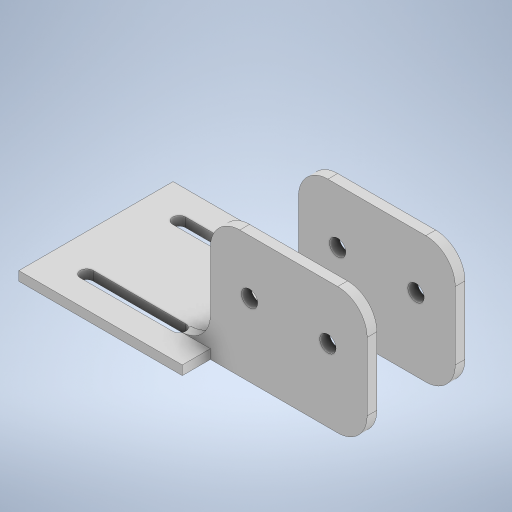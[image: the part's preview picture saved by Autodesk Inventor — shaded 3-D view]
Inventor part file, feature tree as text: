
AUTODESK INVENTOR PART (.ipt)
format: ipt  version: 2024 (Build 280153000, 153)  size: 513,024 bytes
history: native  units: in
note: dims shown in document units (in); Inventor stores cm internally (conversion verified against a paired STEP export)
features: sketch x24, extrude x23, projected_geometry x6, fillet x3
ambient origin geometry x8: Origin, YZ Plane, XZ Plane, XY Plane, X Axis, Y Axis, Z Axis, Center Point
bodies: Solid1 (feature_tree)
feature tree (56):
  extrude  "Extrusion1"  Depth=1.9685in
  extrude  "Extrusion2"  Depth=0.1181in
  extrude  "Extrusion3"  Depth=0.4331in
  extrude  "Extrusion4"  Depth=1.1811in
  extrude  "Extrusion5"  Depth=0.165in
  extrude  "Extrusion6"  Depth=0.165in
  extrude  "Extrusion7"  Depth=0.3935in
  extrude  "Extrusion8"  Depth=0.4921in TaperAngle=0.0deg
  extrude  "Extrusion9"  Depth=0.125in
  extrude  "Extrusion10"  Depth=1.0in
  extrude  "Extrusion11"  Depth=1.667in TaperAngle=0.0deg
  extrude  "Extrusion12"  Depth=1.2705in TaperAngle=0.0deg
  extrude  "Extrusion13"  Depth=0.125in
  extrude  "Extrusion14"  Depth=1.0in
  extrude  "Extrusion15"  Depth=2.9375in TaperAngle=0.0deg
  extrude  "Extrusion16"  Depth=2.0625in TaperAngle=0.0deg
  extrude  "Extrusion17"  Depth=1.0in
  fillet  "Fillet1"  Radius=1.0in
  sketch  "Sketch18"  dims[d48=0.207in d49=0.207in]
  extrude  "Extrusion18"  Depth=0.207in
  sketch  "Sketch20"  dims[d54=1.0in d55=0.4845in]
  extrude  "Extrusion19"  Depth=0.425in TaperAngle=0.0deg
  extrude  "Extrusion20"  Depth=1.0in
  extrude  "Extrusion21"  Depth=0.125in
  fillet  "Fillet2"  Radius=0.125in
  sketch  "Sketch23"  dims[d63=0.375in d64=0.5in d65=1.0in]
  extrude  "Extrusion22"  Depth=1.5in TaperAngle=0.0deg
  extrude  "Extrusion23"  Depth=1.0in
  fillet  "Fillet3"  Radius=1.0in
  sketch  "Sketch1"  dims[d0=2.0866in d1=1.9685in]
  sketch  "Sketch2"  dims[d2=0.1181in d3=0.0in d4=0.1181in]
  sketch  "Sketch3"  dims[d5=2.0079in d6=0.0in d7=0.4331in]
  sketch  "Sketch4"  dims[d8=0.1654in d9=1.1811in]
  sketch  "Sketch5"  dims[d10=0.165in d11=0.433in]
  sketch  "Sketch6"  dims[d12=0.165in d13=0.165in]
  sketch  "Sketch7"  dims[d14=1.1811in d15=0.3935in]
  projected_geometry  "Projected Loop1"
  sketch  "Sketch8"  dims[d16=0.3939in d17=0.4921in d18=0.0in]
  sketch  "Sketch9"  dims[d19=0.875in d20=0.0in d21=0.125in]
  sketch  "Sketch10"  dims[d22=0.125in d23=1.0in]
  sketch  "Sketch11"  dims[d24=0.36in d25=1.667in d26=0.0in]
  projected_geometry  "Projected Loop2"
  projected_geometry  "Projected Loop3"
  sketch  "Sketch12"  dims[d27=0.667in d28=1.2705in d29=0.0in]
  sketch  "Sketch13"  dims[d30=0.125in d31=0.0in d32=0.125in]
  sketch  "Sketch14"  dims[d33=1.0in d34=0.0in d35=0.34in]
  sketch  "Sketch15"  dims[d36=0.4375in d37=0.0in d38=2.9375in d39=0.0in]
  projected_geometry  "Projected Loop4"
  sketch  "Sketch16"  dims[d40=3.3125in d41=0.0in d42=2.0625in d43=0.0in]
  sketch  "Sketch17"  dims[d44=0.425in d45=0.0in d46=0.5in d47=1.0in]
  sketch  "Sketch19"  dims[d50=1.575in d51=0.0in d52=0.425in d53=0.0in]
  sketch  "Sketch21"  dims[d56=0.484in d57=0.125in d58=0.125in]
  sketch  "Sketch22"  dims[d59=1.0in d60=0.0in d61=1.5in d62=0.0in]
  sketch  "Sketch24"  dims[d66=0.207in d67=0.207in d68=7.8125in d69=0.0in d70=0.425in d71=0.5in d72=0.207in d73=0.125in d74=0.0in d75=0.125in d76=0.0in d77=1.875in d78=0.0in d79=0.375in d80=1.0in d81=0.207in d82=1.0in d83=0.0in d84=1.4375in d85=0.0in d86=0.375in]
  projected_geometry  "Projected Loop5"
  projected_geometry  "Projected Loop6"
